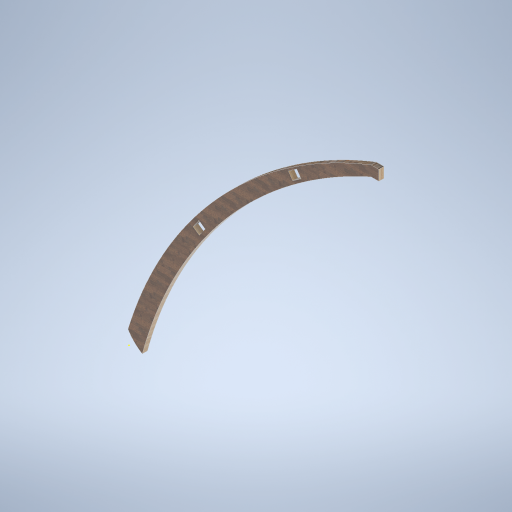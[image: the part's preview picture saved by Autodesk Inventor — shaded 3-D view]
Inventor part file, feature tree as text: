
AUTODESK INVENTOR PART (.ipt)
format: ipt  version: 2024.2 (Build 282272000, 272)  size: 304,128 bytes
history: native  units: mm
features: extrude x2, sketch x2
ambient origin geometry x8: Origin, YZ Plane, XZ Plane, XY Plane, X Axis, Y Axis, Z Axis, Center Point
bodies: Solid1 (feature_tree)
feature tree (4):
  extrude  "Extrusion1"  Depth=200.0mm
  sketch  "Sketch3"  dims[d0=100.0mm d1=0.0mm d2=200.0mm]
  extrude  "Extrusion2"  Depth=150.0mm
  sketch  "Sketch4"  dims[d3=6.108652mm d4=150.0mm d5=200.0mm d6=9.599311mm d7=150.0mm d8=0.0mm d9=0.0mm]
